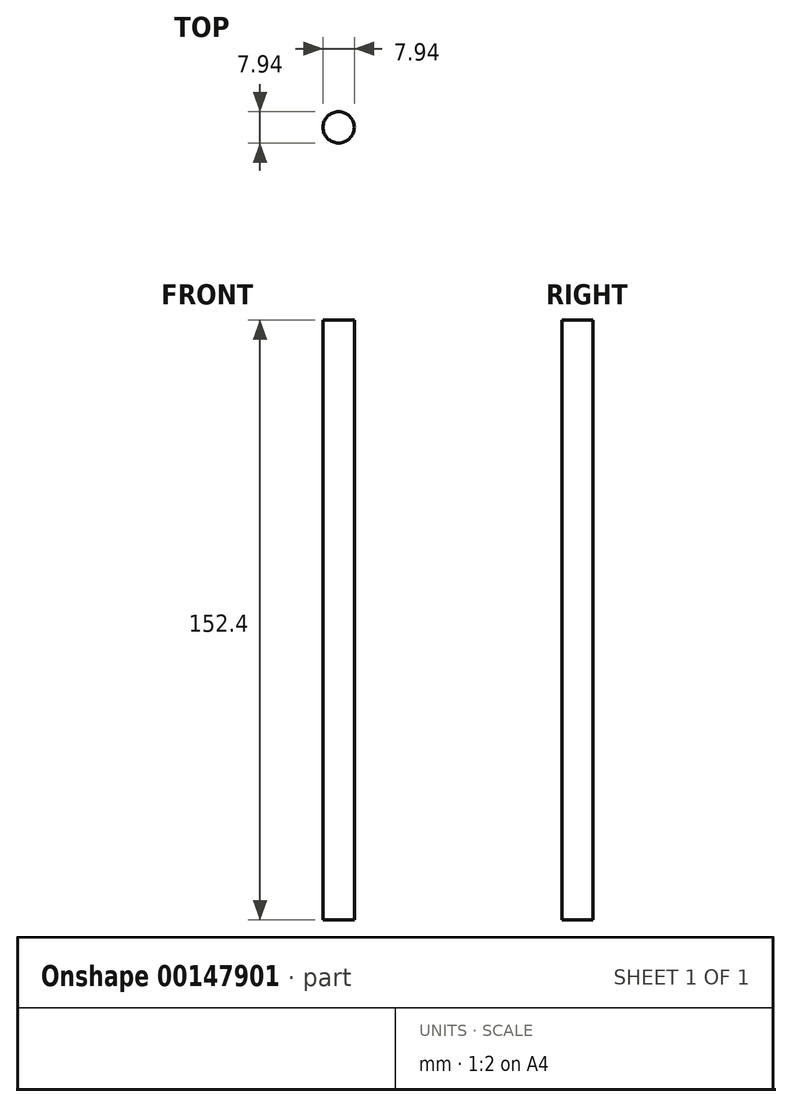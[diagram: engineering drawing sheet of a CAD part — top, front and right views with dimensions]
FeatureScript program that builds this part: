
annotation { "Feature Type Name" : "Feature", "Feature Type Description" : "" }
export const myFeature = defineFeature(function(context is Context, id is Id, definition is map)
    precondition{}
    {
        {
            var Q0;
            Q0=qCreatedBy(makeId("Top.planeOp"),FACE);
            var sketch = newSketch(context, id + "F0", { "sketchPlane" : qUnion([Q0])});
            skCircle(sketch, "E0", {"center": v(0, 0) * mm, "radius": 3.97 * mm});
            skSolve(sketch);
        }
        {
            var Q0;
            Q0=qSketchRegion(id+"F0",true);
            extrude(context, id + "F1", {"entities" : qUnion([Q0]), "depth" : 152.4 * mm});
        }
    });
